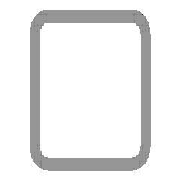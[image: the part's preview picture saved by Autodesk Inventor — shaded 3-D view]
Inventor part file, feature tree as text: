
AUTODESK INVENTOR PART (.ipt)
format: ipt  version: 2025 (Build 290162010, 162A)  size: 133,120 bytes
history: native  units: mm (DEFAULTED — no unit token found)
features: other x4, sketch x1, plane x1
ambient origin geometry x8: Origin, YZ Plane, XZ Plane, XY Plane, X Axis, Y Axis, Z Axis, Center Point
bodies: Solid1 (feature_tree), Body (feature_tree)
feature tree (6):
  parser-record x1  (decoder bookkeeping rows leaked as tree rows — omitted from the tree; the rows remain in map.json)
  other  "Driven Length"
  other  "Start Plane"
  other  "End Plane"
  sketch  "Sketch3"  dims[d3=970.0mm d4=0.0mm d7=6.0mm d9=80.0mm d11=80.0mm d12=3.0mm d13=40.0mm d14=1010.0mm d15=40.0mm d16=40.0mm d17=90.0deg d18=970.0mm]
  plane  "Work Plane3"
